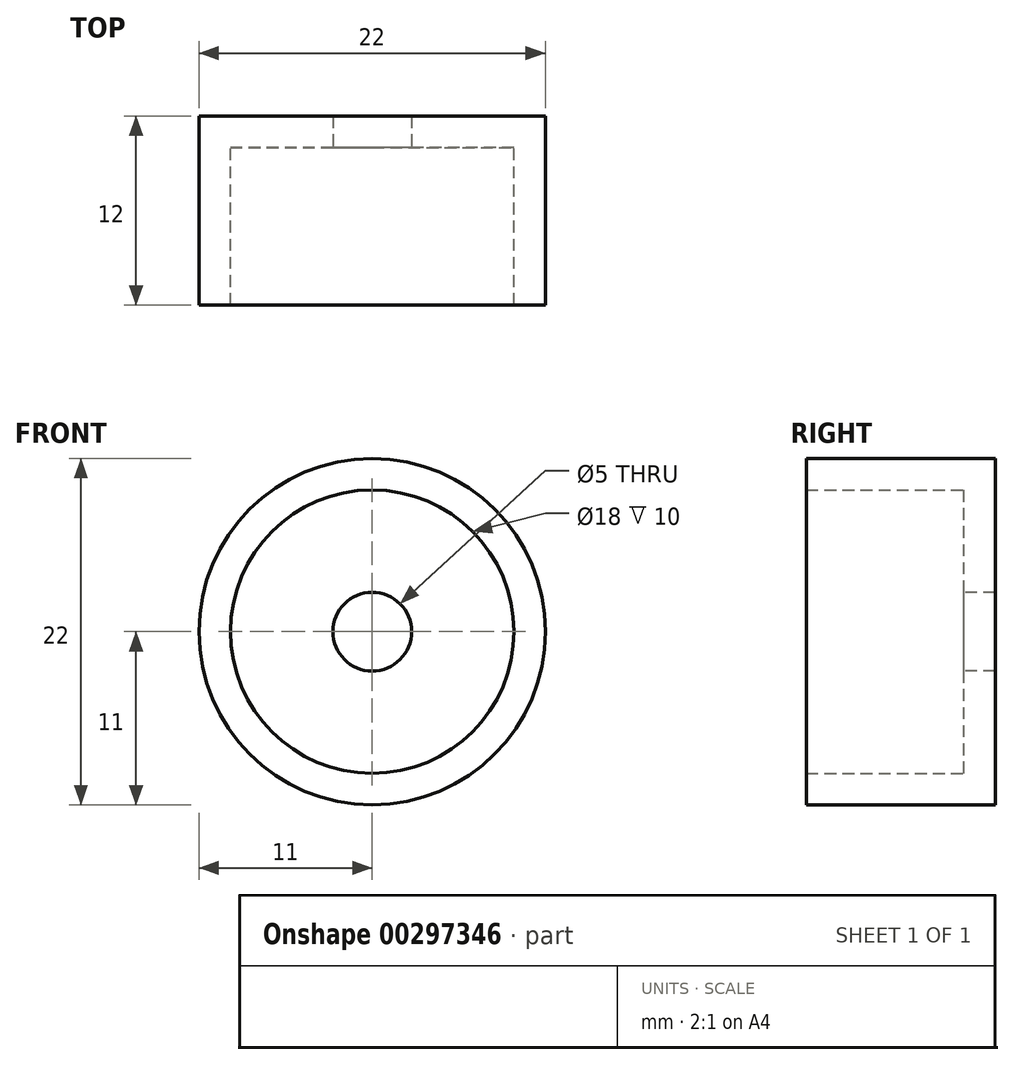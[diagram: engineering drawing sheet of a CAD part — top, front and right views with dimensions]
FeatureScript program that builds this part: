
annotation { "Feature Type Name" : "Feature", "Feature Type Description" : "" }
export const myFeature = defineFeature(function(context is Context, id is Id, definition is map)
    precondition{}
    {
        {
            var Q0;
            Q0=qCreatedBy(makeId("Front.planeOp"),FACE);
            var sketch = newSketch(context, id + "F0", { "sketchPlane" : qUnion([Q0])});
            skCircle(sketch, "E0", {"center": v(0, 0) * mm, "radius": 11 * mm});
            skSolve(sketch);
        }
        {
            var Q0;
            Q0=qSketchRegion(id+"F0",true);
            extrude(context, id + "F1", {"entities" : qUnion([Q0]), "depth" : 2 * mm});
        }
        {
            var Q0;
            Q0=makeQuery(id+"F1.opExtrude","CAP_FACE",FACE,{"disambiguationData":[OSD([sQuery(id+"F0.wireOp",EDGE,"E0")])],"isStart":false});
            var sketch = newSketch(context, id + "F2", { "sketchPlane" : qUnion([Q0])});
            skCircle(sketch, "E1", {"center": v(0, 0) * mm, "radius": 2.5 * mm});
            skSolve(sketch);
        }
        {
            var Q0;
            Q0=qSketchRegion(id+"F2",true);
            extrude(context, id + "F3", {"entities" : qUnion([Q0]), "operationType" : NewBodyOperationType.REMOVE, "oppositeDirection" : true, "depth" : 25 * mm});
        }
        {
            var Q0;
            Q0=makeQuery(id+"F1.opExtrude","CAP_FACE",FACE,{"disambiguationData":[OSD([sQuery(id+"F0.wireOp",EDGE,"E0")])],"isStart":false});
            var sketch = newSketch(context, id + "F4", { "sketchPlane" : qUnion([Q0])});
            skCircle(sketch, "E2", {"center": v(0, 0) * mm, "radius": 11 * mm});
            skCircle(sketch, "E3", {"center": v(0, 0) * mm, "radius": 9 * mm});
            skSolve(sketch);
        }
        {
            var Q0;
            Q0=qSketchRegion(id+"F4",true);
            extrude(context, id + "F5", {"entities" : qUnion([Q0]), "operationType" : NewBodyOperationType.ADD, "depth" : 10 * mm});
        }
    });
